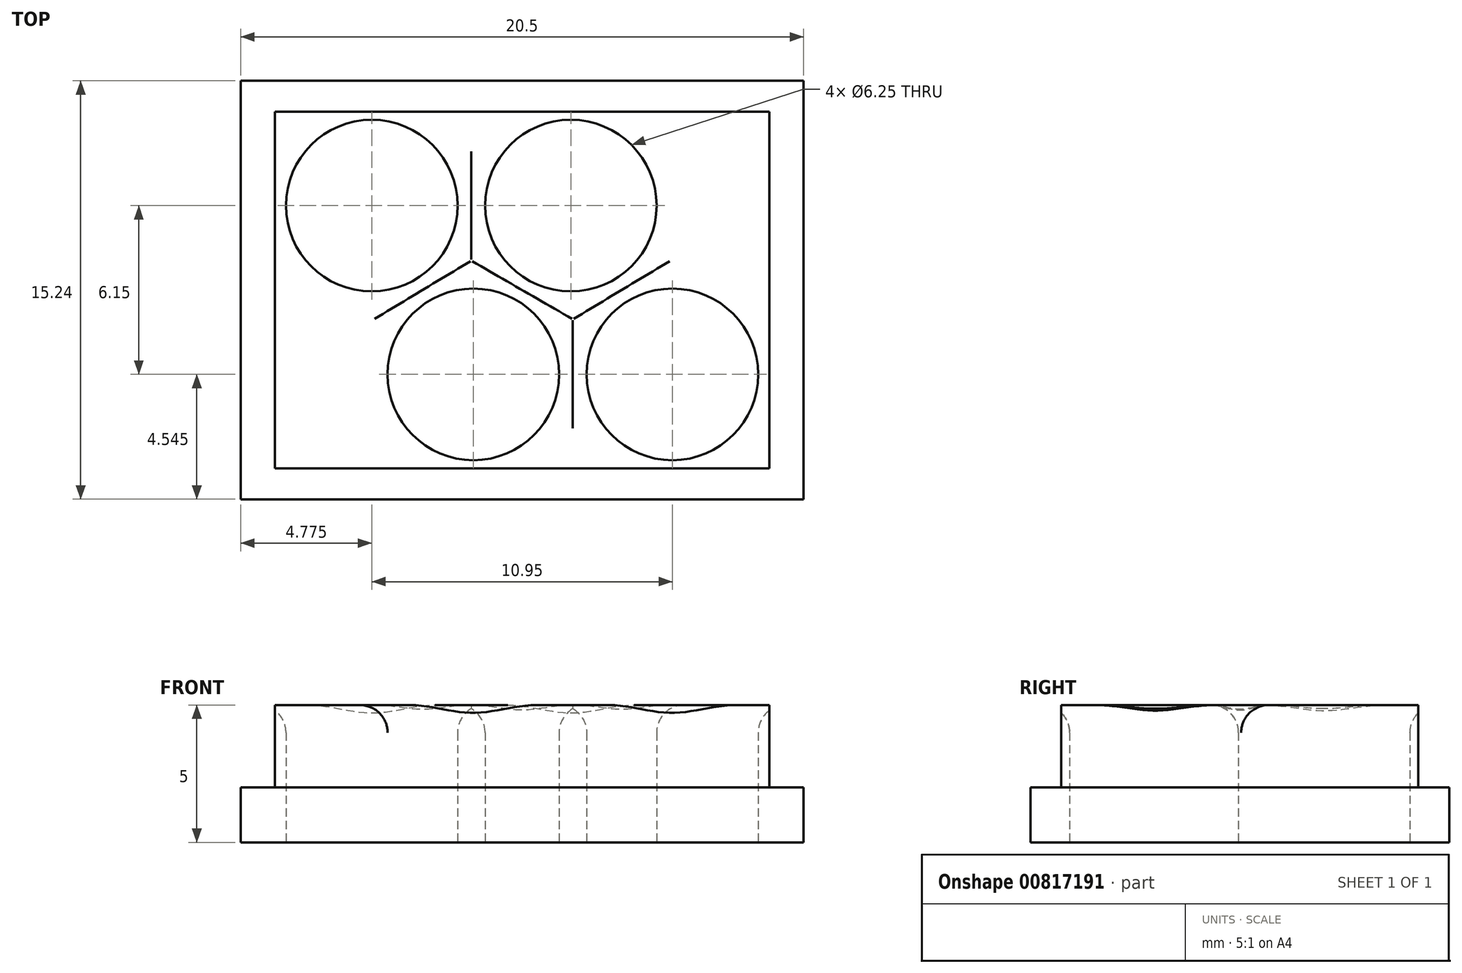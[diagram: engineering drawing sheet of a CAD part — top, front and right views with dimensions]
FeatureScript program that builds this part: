
annotation { "Feature Type Name" : "Feature", "Feature Type Description" : "" }
export const myFeature = defineFeature(function(context is Context, id is Id, definition is map)
    precondition{}
    {
        {
            var Q0;
            Q0=qCreatedBy(makeId("Top.planeOp"),FACE);
            var sketch = newSketch(context, id + "F0", { "sketchPlane" : qUnion([Q0])});
            skLineSegment(sketch, "E0.bottom", {"start": v(10.25, 7.63) * mm, "end": v(-10.25, 7.63) * mm});
            skLineSegment(sketch, "E0.top", {"start": v(10.25, -7.63) * mm, "end": v(-10.25, -7.63) * mm});
            skLineSegment(sketch, "E0.left", {"start": v(10.25, 7.63) * mm, "end": v(10.25, -7.63) * mm});
            skLineSegment(sketch, "E0.right", {"start": v(-10.25, 7.63) * mm, "end": v(-10.25, -7.63) * mm});
            skPoint(sketch, "E0.middle", {"position": v(0, 0) * mm});
            skLineSegment(sketch, "E1.bottom", {"start": v(-9, 6.5) * mm, "end": v(9, 6.5) * mm});
            skLineSegment(sketch, "E1.top", {"start": v(-9, -6.5) * mm, "end": v(9, -6.5) * mm});
            skLineSegment(sketch, "E1.left", {"start": v(-9, 6.5) * mm, "end": v(-9, -6.5) * mm});
            skLineSegment(sketch, "E1.right", {"start": v(9, 6.5) * mm, "end": v(9, -6.5) * mm});
            skCircle(sketch, "E2", {"center": v(-5.48, 3.08) * mm, "radius": 3.12 * mm});
            skCircle(sketch, "E3", {"center": v(-1.77, -3.08) * mm, "radius": 3.12 * mm});
            skCircle(sketch, "E4", {"center": v(5.48, -3.08) * mm, "radius": 3.12 * mm});
            skCircle(sketch, "E5", {"center": v(1.77, 3.08) * mm, "radius": 3.12 * mm});
            skLineSegment(sketch, "E6", {"start": v(-5.48, 3.08) * mm, "end": v(1.77, 3.08) * mm, "construction": true});
            skLineSegment(sketch, "E7", {"start": v(-1.77, -3.08) * mm, "end": v(5.48, -3.08) * mm, "construction": true});
            skSolve(sketch);
        }
        {
            var Q0;
            Q0=makeQuery(id+"F0.imprint","IMPRINT",FACE,{"disambiguationData":[TD([[makeQuery(id+"F0.imprint","IMPRINT",EDGE,{"derivedFrom":sQuery(id+"F0.wireOp",EDGE,"E0.bottom")}),1.0]])]});
            var Q1;
            Q1=makeQuery(id+"F0.imprint","IMPRINT",FACE,{"disambiguationData":[TD([[makeQuery(id+"F0.imprint","IMPRINT",EDGE,{"derivedFrom":sQuery(id+"F0.wireOp",EDGE,"E1.bottom")}),-1.0]])]});
            extrude(context, id + "F1", {"entities" : qUnion([Q0, Q1]), "depth" : 2 * mm, "offsetDistance" : 25 * mm});
        }
        {
            var Q0;
            Q0=makeQuery(id+"F0.imprint","IMPRINT",FACE,{"disambiguationData":[TD([[makeQuery(id+"F0.imprint","IMPRINT",EDGE,{"derivedFrom":sQuery(id+"F0.wireOp",EDGE,"E1.bottom")}),-1.0]])]});
            extrude(context, id + "F2", {"entities" : qUnion([Q0]), "operationType" : NewBodyOperationType.ADD, "depth" : 5 * mm, "offsetDistance" : 25 * mm});
        }
        {
            var Q0;
            Q0=makeQuery(id+"F2.opExtrude","CAP_EDGE",EDGE,{"disambiguationData":[OSD([sQuery(id+"F0.wireOp",EDGE,"E2")])],"isStart":false});
            var Q1;
            Q1=makeQuery(id+"F2.opExtrude","CAP_EDGE",EDGE,{"disambiguationData":[OSD([sQuery(id+"F0.wireOp",EDGE,"E5")])],"isStart":false});
            var Q2;
            Q2=makeQuery(id+"F2.opExtrude","CAP_EDGE",EDGE,{"disambiguationData":[OSD([sQuery(id+"F0.wireOp",EDGE,"E3")])],"isStart":false});
            var Q3;
            Q3=makeQuery(id+"F2.opExtrude","CAP_EDGE",EDGE,{"disambiguationData":[OSD([sQuery(id+"F0.wireOp",EDGE,"E4")])],"isStart":false});
            fillet(context, id + "F3", {"entities" : qUnion([Q0, Q1, Q2, Q3]), "radius" : 1 * mm, "tangentPropagation" : true, "allowEdgeOverflow" : false});
        }
    });
